# Revit family: SANINDUSA_131320004_Easy_60Easywall-hungbasin610x465x186_V0
name_source: partatom
category: Plumbing Fixtures
revit_build: Autodesk Revit 2018 (Build: 20170223_1515(x64)
units: mm (PartAtom-declared; Revit-internal decimal feet)

## family parameters
Cut with Voids When Loaded = No
Host = Face
Part Type = Normal
Room Calculation Point = No
Round Connector Dimension = Use Diameter
Shared = No

## types (1)
- SANINDUSA_131320004_Easy_60Easywall-hungbasin610x465x186_V0
    AssetType = Fixed
    Category = Pr_40_20_96_18: Counter top wash basins
    CodePerformance = EN 14688:2015 CL 25
    Color = white
    Constituents = Includes Fixing Kit
    Default Elevation = 1219 mm
    Description = Waste water appliance for washing the upper parts of the body.
    DrainSize = 46 mm  [stored 0.150919 ft]
    Element Type = WASHHANDBASIN: Waste water appliance for washing the upper parts of the body.
    Features = "Installation wall-mounted. Glazed on all sides. Without embellisher ring"
    Finish = gloss
    Installation Instructions = https://www.tec.sanindusa.pt
    InstallationDate = 1900-12-31T23:59:59
    Manufacturer = Sanindusa
    ManufacturerName = Sanindusa
    ManufacturerURL = www.tec.sanindusa.pt
    Material = vitreous china
    Model = 131320004
    ModelNumber = 131320004
    ModelReference = Easy
    Name = 60 Easy washbasin
    NominalDepth = 140 mm  [stored 0.459318 ft]
    NominalHeight = 186 mm  [stored 0.610236 ft]
    NominalLength = 610 mm  [stored 2.00131 ft]
    NominalWidth = 465 mm  [stored 1.52559 ft]
    Pre-defined type (IFC) = WASHHANDBASIN
    ProductInformation = https://www.tec.sanindusa.pt
    ProductionYear = 2012
    Shape = round
    Size = 610x465x186
    SpilloverLevel = 55
    Type (IFC) = IfcSanitaryTerminalType
    URL = www.tec.sanindusa.pt
    Uniclass2015Code = Pr_40_20_96_18
    Uniclass2015Title = Counter top wash basins
    Uniclass2015Version = Products v1.6
    Version = 1
    WarrantyDescription = https://www.tec.sanindusa.pt
    WarrantyDurationParts = 5
    WarrantyDurationUnit = year
    WarrantyStartDate = 1900-12-31T23:59:59
    WashHandBasinMounting = wallhung
    WashHandBasinType = handrinse
    Waste Connection = Yes
    Weight = 14.20 kg

note: [stored X ft] marks values corroborated as IEEE doubles in the binary element streams (Revit-internal decimal feet)

## geometry (parser evidence)
native form markers: Sweep x6
no freeform markers — native parametric forms only
